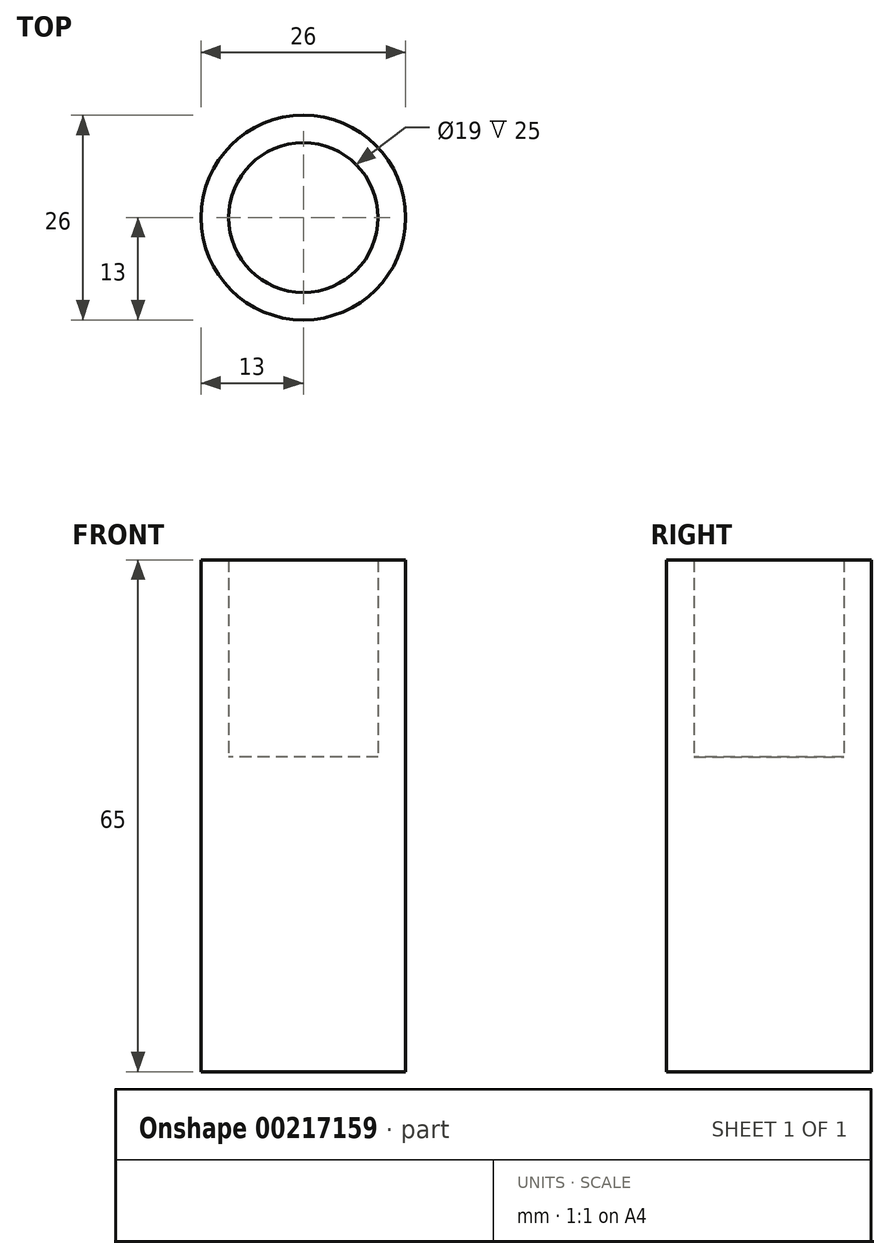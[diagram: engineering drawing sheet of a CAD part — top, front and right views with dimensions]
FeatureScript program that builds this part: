
annotation { "Feature Type Name" : "Feature", "Feature Type Description" : "" }
export const myFeature = defineFeature(function(context is Context, id is Id, definition is map)
    precondition{}
    {
        {
            var Q0;
            Q0=qCreatedBy(makeId("Top.planeOp"),FACE);
            var sketch = newSketch(context, id + "F0", { "sketchPlane" : qUnion([Q0])});
            skCircle(sketch, "E0", {"center": v(0, 0) * mm, "radius": 13 * mm});
            skSolve(sketch);
        }
        {
            var Q0;
            Q0=makeQuery(id+"F0.imprint","IMPRINT",FACE,{"disambiguationData":[TD([[makeQuery(id+"F0.imprint","IMPRINT",EDGE,{"derivedFrom":sQuery(id+"F0.wireOp",EDGE,"E0")}),1.0]])]});
            extrude(context, id + "F1", {"entities" : qUnion([Q0]), "depth" : 40 * mm});
        }
        {
            var Q0;
            Q0=makeQuery(id+"F1.opExtrude","CAP_FACE",FACE,{"disambiguationData":[OSD([sQuery(id+"F0.wireOp",EDGE,"E0")])],"isStart":false});
            var sketch = newSketch(context, id + "F2", { "sketchPlane" : qUnion([Q0])});
            skCircle(sketch, "E1", {"center": v(0, 0) * mm, "radius": 9.5 * mm});
            skCircle(sketch, "E2.0", {"center": v(0, 0) * mm, "radius": 13 * mm});
            skSolve(sketch);
        }
        {
            var Q0;
            Q0 = qSketchRegion(id + "F2", true);
            extrude(context, id + "F3", {"entities" : qUnion([Q0]), "operationType" : NewBodyOperationType.ADD, "depth" : 25 * mm});
        }
    });
